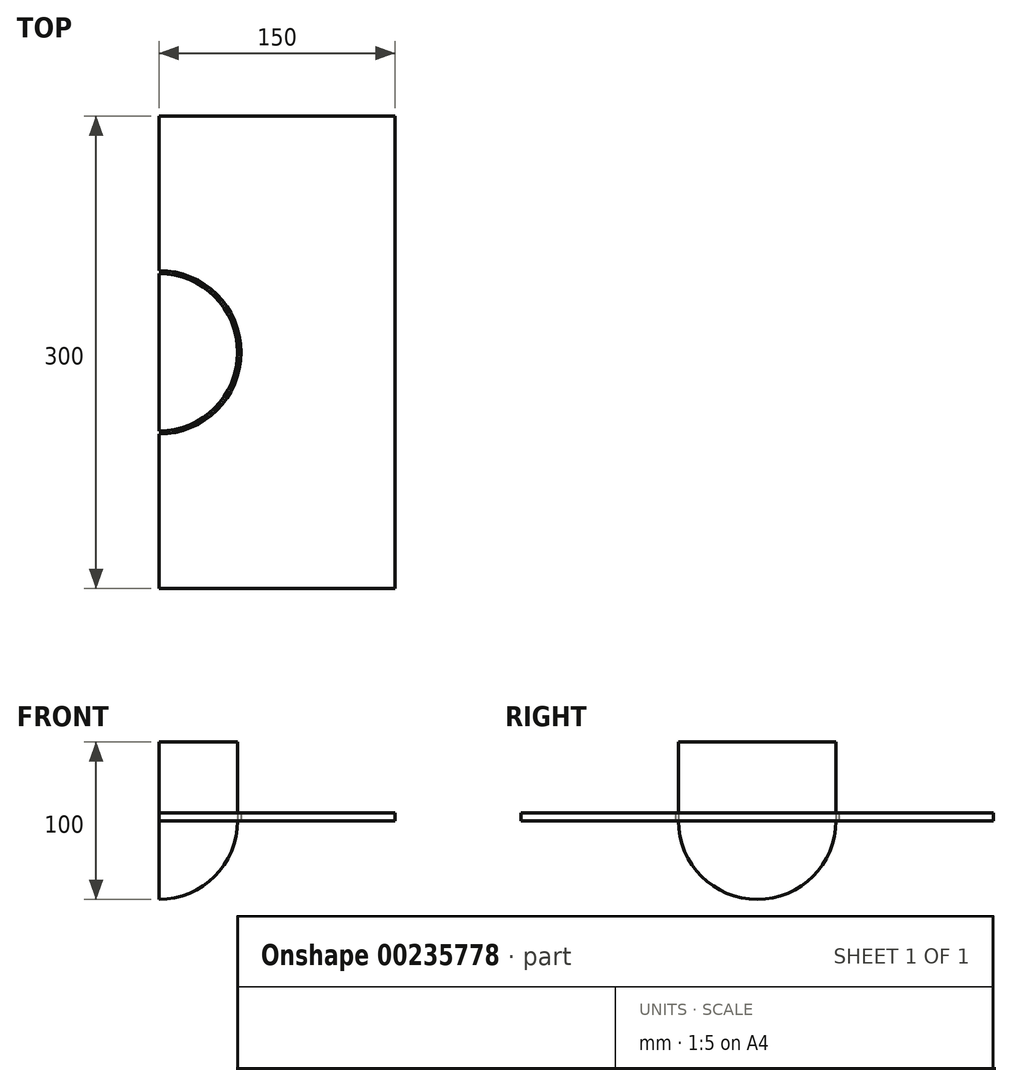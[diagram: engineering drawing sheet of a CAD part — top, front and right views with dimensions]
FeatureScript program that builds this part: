
annotation { "Feature Type Name" : "Feature", "Feature Type Description" : "" }
export const myFeature = defineFeature(function(context is Context, id is Id, definition is map)
    precondition{}
    {
        {
            var Q0;
            Q0=qCreatedBy(makeId("Right.planeOp"),FACE);
            var sketch = newSketch(context, id + "F0", { "sketchPlane" : qUnion([Q0])});
            skLineSegment(sketch, "E0", {"start": v(0, 0) * mm, "end": v(0, -50) * mm});
            skArc(sketch, "E1", {"start": v(0, -50) * mm, "mid": v(35.36, -35.36) * mm, "end": v(50, 0) * mm});
            skLineSegment(sketch, "E2", {"start": v(0, 0) * mm, "end": v(50, 0) * mm});
            skSolve(sketch);
        }
        {
            var Q0;
            Q0=makeQuery(id+"F0.imprint","IMPRINT",FACE,{"disambiguationData":[TD([[makeQuery(id+"F0.imprint","IMPRINT",EDGE,{"derivedFrom":sQuery(id+"F0.wireOp",EDGE,"E0")}),1.0]])]});
            var Q1;
            Q1=sQuery(id+"F0.wireOp",EDGE,"E0");
            revolve(context, id + "F1", {"entities" : qUnion([Q0]), "axis" : qUnion([Q1]), "revolveType" : RevolveType.ONE_DIRECTION, "angle" : 180 * degree});
        }
        {
            var Q0;
            Q0=makeQuery(id+"F1.opRevolve","SWEPT_FACE",FACE,{"disambiguationData":[OSD([sQuery(id+"F0.wireOp",EDGE,"E2")])]});
            extrude(context, id + "F2", {"entities" : qUnion([Q0]), "operationType" : NewBodyOperationType.ADD, "depth" : 50 * mm});
        }
        {
            var Q0;
            Q0=qCreatedBy(makeId("Top.planeOp"),FACE);
            var sketch = newSketch(context, id + "F3", { "sketchPlane" : qUnion([Q0])});
            skLineSegment(sketch, "E3", {"start": v(0, -52) * mm, "end": v(0, -150) * mm});
            skLineSegment(sketch, "E4", {"start": v(0, -150) * mm, "end": v(150, -150) * mm});
            skLineSegment(sketch, "E5", {"start": v(150, -150) * mm, "end": v(150, 150) * mm});
            skLineSegment(sketch, "E6", {"start": v(150, 150) * mm, "end": v(0, 150) * mm});
            skLineSegment(sketch, "E7", {"start": v(0, 150) * mm, "end": v(0, 52) * mm});
            skArc(sketch, "E8", {"start": v(0, -52) * mm, "mid": v(52, 0) * mm, "end": v(0, 52) * mm});
            skSolve(sketch);
        }
        {
            var Q0;
            Q0=makeQuery(id+"F3.imprint","IMPRINT",FACE,{"disambiguationData":[TD([[makeQuery(id+"F3.imprint","IMPRINT",EDGE,{"derivedFrom":sQuery(id+"F3.wireOp",EDGE,"E3")}),1.0]])]});
            extrude(context, id + "F4", {"entities" : qUnion([Q0]), "depth" : 5 * mm});
        }
    });
